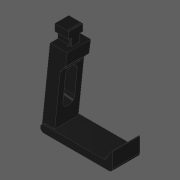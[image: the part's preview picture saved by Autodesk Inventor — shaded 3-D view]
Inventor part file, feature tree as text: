
AUTODESK INVENTOR PART (.ipt)
format: ipt  version: 2020 (Build 240168000, 168)  size: 340,992 bytes
history: native  units: in
note: dims shown in document units (in); Inventor stores cm internally (conversion verified against a paired STEP export)
features: extrude x5, other x3
ambient origin geometry x8: Origin, YZ Plane, XZ Plane, XY Plane, X Axis, Y Axis, Z Axis, Center Point
bodies: Solid1 (feature_tree)
feature tree (8):
  other  "Neck Start Plane"
  other  "Arm Profile"
  extrude  "Main Arm"  Depth=0.0049in
  extrude  "Pincher"  Depth=1.0534in
  extrude  "Neck"  Depth=0.7283in
  extrude  "Spring Steel Slot"  Depth=0.1181in
  extrude  "Viewport"  TaperAngle=0.0deg  [1 undecoded]
  other  "Neck Sketch"
note: 1 required parameter value undecoded (feature->parameter linkage not recoverable at this tier; creation-order binding heuristic only, values carry confidence <= 0.55)
